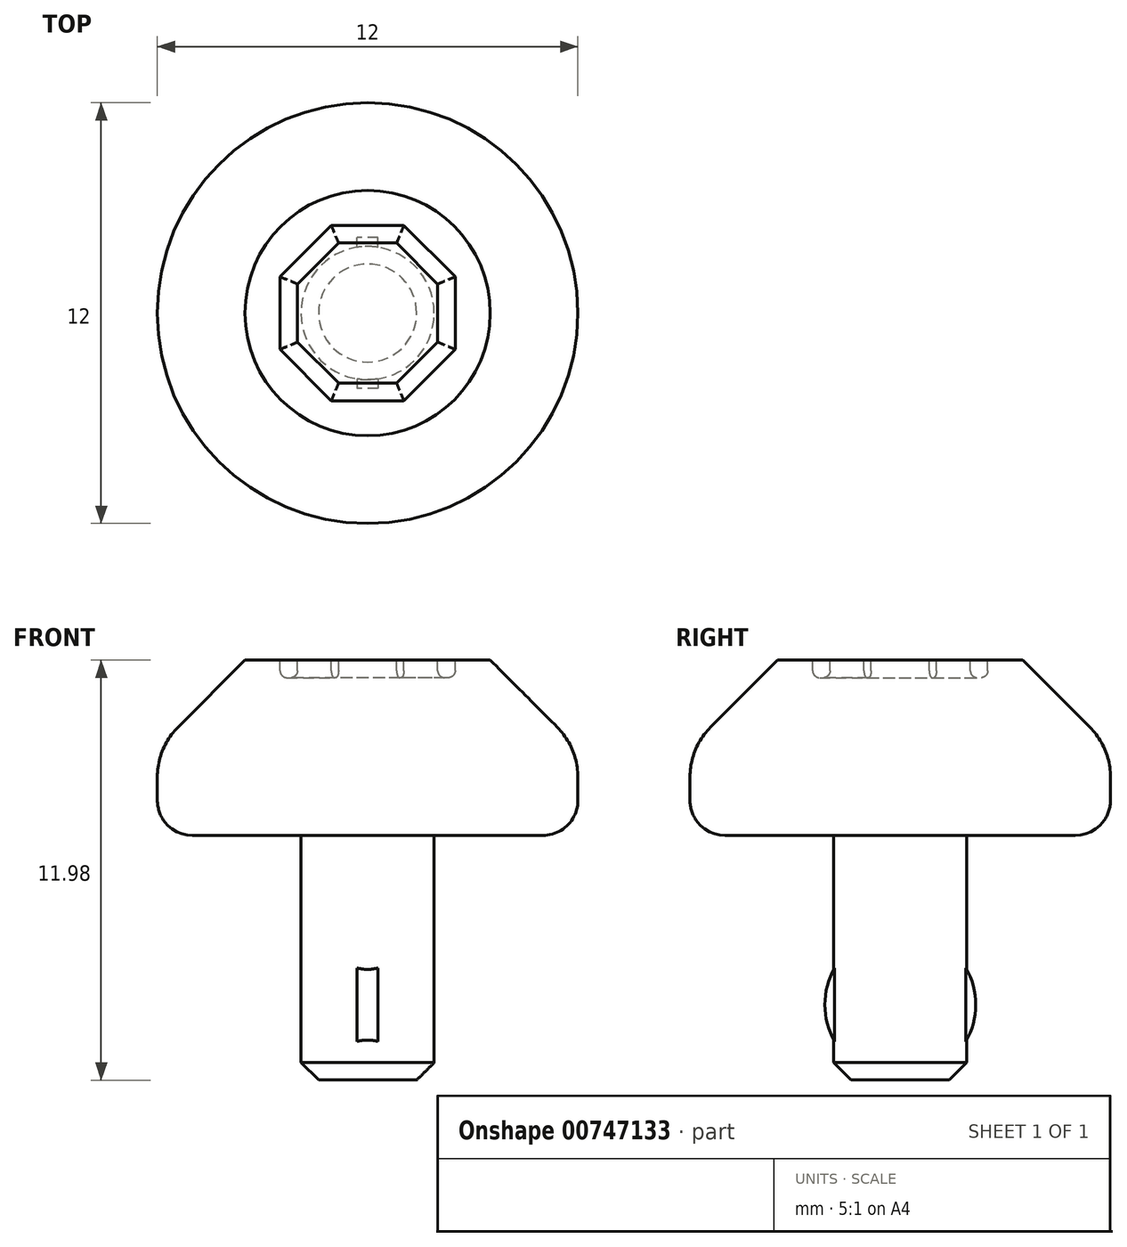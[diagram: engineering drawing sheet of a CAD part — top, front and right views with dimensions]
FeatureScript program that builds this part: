
annotation { "Feature Type Name" : "Feature", "Feature Type Description" : "" }
export const myFeature = defineFeature(function(context is Context, id is Id, definition is map)
    precondition{}
    {
        {
            var Q0;
            Q0=qCreatedBy(makeId("Front.planeOp"),FACE);
            var sketch = newSketch(context, id + "F0", { "sketchPlane" : qUnion([Q0])});
            skLineSegment(sketch, "E0", {"start": v(0, -9.48) * mm, "end": v(-1.9, -9.48) * mm});
            skLineSegment(sketch, "E1", {"start": v(-1.9, -9.48) * mm, "end": v(-1.9, -2.5) * mm});
            skLineSegment(sketch, "E2", {"start": v(-1.9, -2.5) * mm, "end": v(-6, -2.5) * mm});
            skLineSegment(sketch, "E3", {"start": v(-6, -2.5) * mm, "end": v(-6, 0) * mm});
            skLineSegment(sketch, "E4", {"start": v(-6, 0) * mm, "end": v(-3.5, 2.5) * mm});
            skLineSegment(sketch, "E5", {"start": v(-3.5, 2.5) * mm, "end": v(0, 2.5) * mm});
            skLineSegment(sketch, "E6", {"start": v(0, 2.5) * mm, "end": v(0, -9.48) * mm});
            skSolve(sketch);
        }
        {
            var Q0;
            Q0=makeQuery(id+"F0.imprint","IMPRINT",FACE,{"disambiguationData":[TD([[makeQuery(id+"F0.imprint","IMPRINT",EDGE,{"derivedFrom":sQuery(id+"F0.wireOp",EDGE,"E0")}),-1.0]])]});
            var Q1;
            Q1=sQuery(id+"F0.wireOp",EDGE,"E6");
            revolve(context, id + "F1", {"surfaceOperationType" : NewSurfaceOperationType.NEW, "entities" : qUnion([Q0]), "axis" : qUnion([Q1]), "revolveType" : RevolveType.FULL});
        }
        {
            var Q0;
            Q0=makeQuery(id+"F1.opRevolve","SWEPT_EDGE",EDGE,{"disambiguationData":[OSD([sQuery(id+"F0.wireOp",EDGE,"E3"),sQuery(id+"F0.wireOp",EDGE,"E4")])]});
            fillet(context, id + "F2", {"entities" : qUnion([Q0]), "radius" : 2 * mm, "tangentPropagation" : true, "allowEdgeOverflow" : false});
        }
        {
            var Q0;
            Q0=makeQuery(id+"F1.opRevolve","SWEPT_EDGE",EDGE,{"disambiguationData":[OSD([sQuery(id+"F0.wireOp",EDGE,"E2"),sQuery(id+"F0.wireOp",EDGE,"E3")])]});
            fillet(context, id + "F3", {"entities" : qUnion([Q0]), "radius" : 1 * mm, "tangentPropagation" : true, "allowEdgeOverflow" : false});
        }
        {
            var Q0;
            Q0=qCreatedBy(makeId("Right.planeOp"),FACE);
            var sketch = newSketch(context, id + "F4", { "sketchPlane" : qUnion([Q0])});
            skCircle(sketch, "E7", {"center": v(0, -7.33) * mm, "radius": 2.15 * mm});
            skSolve(sketch);
        }
        {
            var Q0;
            Q0=makeQuery(id+"F4.imprint","IMPRINT",FACE,{"disambiguationData":[TD([[makeQuery(id+"F4.imprint","IMPRINT",EDGE,{"derivedFrom":sQuery(id+"F4.wireOp",EDGE,"E7")}),1.0]])]});
            extrude(context, id + "F5", {"entities" : qUnion([Q0]), "operationType" : NewBodyOperationType.ADD, "endBound" : BoundingType.SYMMETRIC, "depth" : 0.6 * mm, "offsetDistance" : 25 * mm});
        }
        {
            var Q0;
            Q0=makeQuery(id+"F1.opRevolve","SWEPT_FACE",FACE,{"disambiguationData":[OSD([sQuery(id+"F0.wireOp",EDGE,"E5")])]});
            var sketch = newSketch(context, id + "F6", { "sketchPlane" : qUnion([Q0])});
            skCircle(sketch, "E8.cCircle", {"center": v(0, 0) * mm, "radius": 2.5 * mm, "construction": true});
            skLineSegment(sketch, "E8.0", {"start": v(-2.5, 1.04) * mm, "end": v(-1.04, 2.5) * mm});
            skLineSegment(sketch, "E8.1", {"start": v(-1.04, 2.5) * mm, "end": v(1.04, 2.5) * mm});
            skLineSegment(sketch, "E8.2", {"start": v(1.04, 2.5) * mm, "end": v(2.5, 1.04) * mm});
            skLineSegment(sketch, "E8.3", {"start": v(2.5, 1.04) * mm, "end": v(2.5, -1.04) * mm});
            skLineSegment(sketch, "E8.4", {"start": v(2.5, -1.04) * mm, "end": v(1.04, -2.5) * mm});
            skLineSegment(sketch, "E8.5", {"start": v(1.04, -2.5) * mm, "end": v(-1.04, -2.5) * mm});
            skLineSegment(sketch, "E8.6", {"start": v(-1.04, -2.5) * mm, "end": v(-2.5, -1.04) * mm});
            skLineSegment(sketch, "E8.7", {"start": v(-2.5, -1.04) * mm, "end": v(-2.5, 1.04) * mm});
            skPoint(sketch, "E8.0.midPoint", {"position": v(-1.77, 1.77) * mm});
            skLineSegment(sketch, "E9.0", {"start": v(-2, 0.83) * mm, "end": v(-0.83, 2) * mm});
            skLineSegment(sketch, "E9.1", {"start": v(-2, -0.83) * mm, "end": v(-2, 0.83) * mm});
            skLineSegment(sketch, "E9.2", {"start": v(-0.83, 2) * mm, "end": v(0.83, 2) * mm});
            skLineSegment(sketch, "E9.3", {"start": v(-0.83, -2) * mm, "end": v(-2, -0.83) * mm});
            skLineSegment(sketch, "E9.4", {"start": v(0.83, 2) * mm, "end": v(2, 0.83) * mm});
            skLineSegment(sketch, "E9.5", {"start": v(2, 0.83) * mm, "end": v(2, -0.83) * mm});
            skLineSegment(sketch, "E9.6", {"start": v(2, -0.83) * mm, "end": v(0.83, -2) * mm});
            skLineSegment(sketch, "E9.7", {"start": v(0.83, -2) * mm, "end": v(-0.83, -2) * mm});
            skSolve(sketch);
        }
        {
            var Q0;
            Q0=makeQuery(id+"F6.imprint","IMPRINT",FACE,{"disambiguationData":[TD([[makeQuery(id+"F6.imprint","IMPRINT",EDGE,{"derivedFrom":sQuery(id+"F6.wireOp",EDGE,"E8.0")}),-1.0]])]});
            extrude(context, id + "F7", {"entities" : qUnion([Q0]), "operationType" : NewBodyOperationType.REMOVE, "oppositeDirection" : true, "depth" : 0.5 * mm, "offsetDistance" : 25 * mm});
        }
        {
            var Q0;
            Q0=makeQuery(id+"F7.boolean.opBoolean","COPY",FACE,{"derivedFrom":makeQuery(id+"F7.opExtrude","CAP_FACE",FACE,{"disambiguationData":[OSD([sQuery(id+"F6.wireOp",EDGE,"E8.0"),sQuery(id+"F6.wireOp",EDGE,"E8.1"),sQuery(id+"F6.wireOp",EDGE,"E8.2"),sQuery(id+"F6.wireOp",EDGE,"E8.3"),sQuery(id+"F6.wireOp",EDGE,"E8.4"),sQuery(id+"F6.wireOp",EDGE,"E8.5"),sQuery(id+"F6.wireOp",EDGE,"E8.6"),sQuery(id+"F6.wireOp",EDGE,"E8.7"),sQuery(id+"F6.wireOp",EDGE,"E9.0"),sQuery(id+"F6.wireOp",EDGE,"E9.1"),sQuery(id+"F6.wireOp",EDGE,"E9.2"),sQuery(id+"F6.wireOp",EDGE,"E9.3"),sQuery(id+"F6.wireOp",EDGE,"E9.4"),sQuery(id+"F6.wireOp",EDGE,"E9.5"),sQuery(id+"F6.wireOp",EDGE,"E9.6"),sQuery(id+"F6.wireOp",EDGE,"E9.7")])],"isStart":false})});
            fillet(context, id + "F8", {"entities" : qUnion([Q0]), "radius" : 0.2 * mm, "tangentPropagation" : true, "allowEdgeOverflow" : false});
        }
        {
            var Q0;
            Q0=makeQuery(id+"F1.opRevolve","SWEPT_EDGE",EDGE,{"disambiguationData":[OSD([sQuery(id+"F0.wireOp",EDGE,"E0"),sQuery(id+"F0.wireOp",EDGE,"E1")])]});
            chamfer(context, id + "F9", {"entities" : qUnion([Q0]), "width" : 0.5 * mm, "tangentPropagation" : true});
        }
    });
